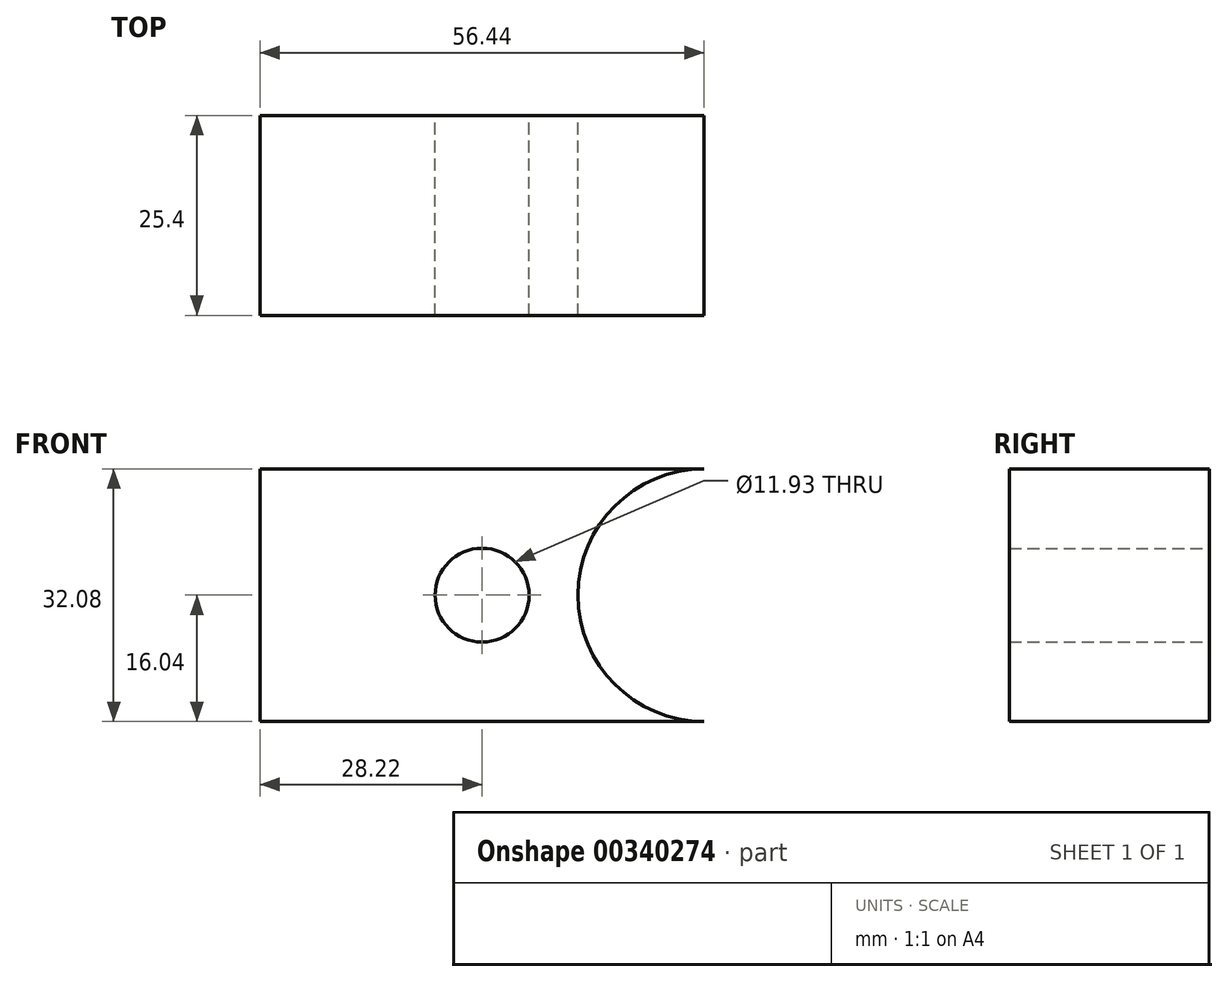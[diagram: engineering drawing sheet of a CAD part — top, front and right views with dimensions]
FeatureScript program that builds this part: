
annotation { "Feature Type Name" : "Feature", "Feature Type Description" : "" }
export const myFeature = defineFeature(function(context is Context, id is Id, definition is map)
    precondition{}
    {
        {
            var Q0;
            Q0=qCreatedBy(makeId("Front.planeOp"),FACE);
            var sketch = newSketch(context, id + "F0", { "sketchPlane" : qUnion([Q0])});
            skLineSegment(sketch, "E0.bottom", {"start": v(12.95, -4.45) * mm, "end": v(13.14, -4.45) * mm});
            skLineSegment(sketch, "E0.top", {"start": v(12.95, -10.82) * mm, "end": v(13.14, -10.82) * mm});
            skLineSegment(sketch, "E1.bottom", {"start": v(-28.22, 16.04) * mm, "end": v(28.22, 16.04) * mm});
            skLineSegment(sketch, "E1.top", {"start": v(-28.22, -16.04) * mm, "end": v(28.22, -16.04) * mm});
            skLineSegment(sketch, "E1.left", {"start": v(-28.22, 16.04) * mm, "end": v(-28.22, -16.04) * mm});
            skLineSegment(sketch, "E1.right", {"start": v(28.22, 16.04) * mm, "end": v(28.22, -16.04) * mm});
            skPoint(sketch, "E1.middle", {"position": v(0, 0) * mm});
            skCircle(sketch, "E2", {"center": v(28.22, 0) * mm, "radius": 16.04 * mm});
            skCircle(sketch, "E3", {"center": v(0, 0) * mm, "radius": 5.97 * mm});
            skSolve(sketch);
        }
        {
            var Q0;
            {var subQ2=sQuery(id+"F0.wireOp",EDGE,"E1.bottom");Q0=makeQuery(id+"F0.imprint","IMPRINT",FACE,{"disambiguationData":[TD([[makeQuery(id+"F0.imprint","IMPRINT",EDGE,{"derivedFrom":subQ2}),-1.0]])]});}
            extrude(context, id + "F1", {"entities" : qUnion([Q0]), "depth" : 25.4 * mm});
        }
    });
